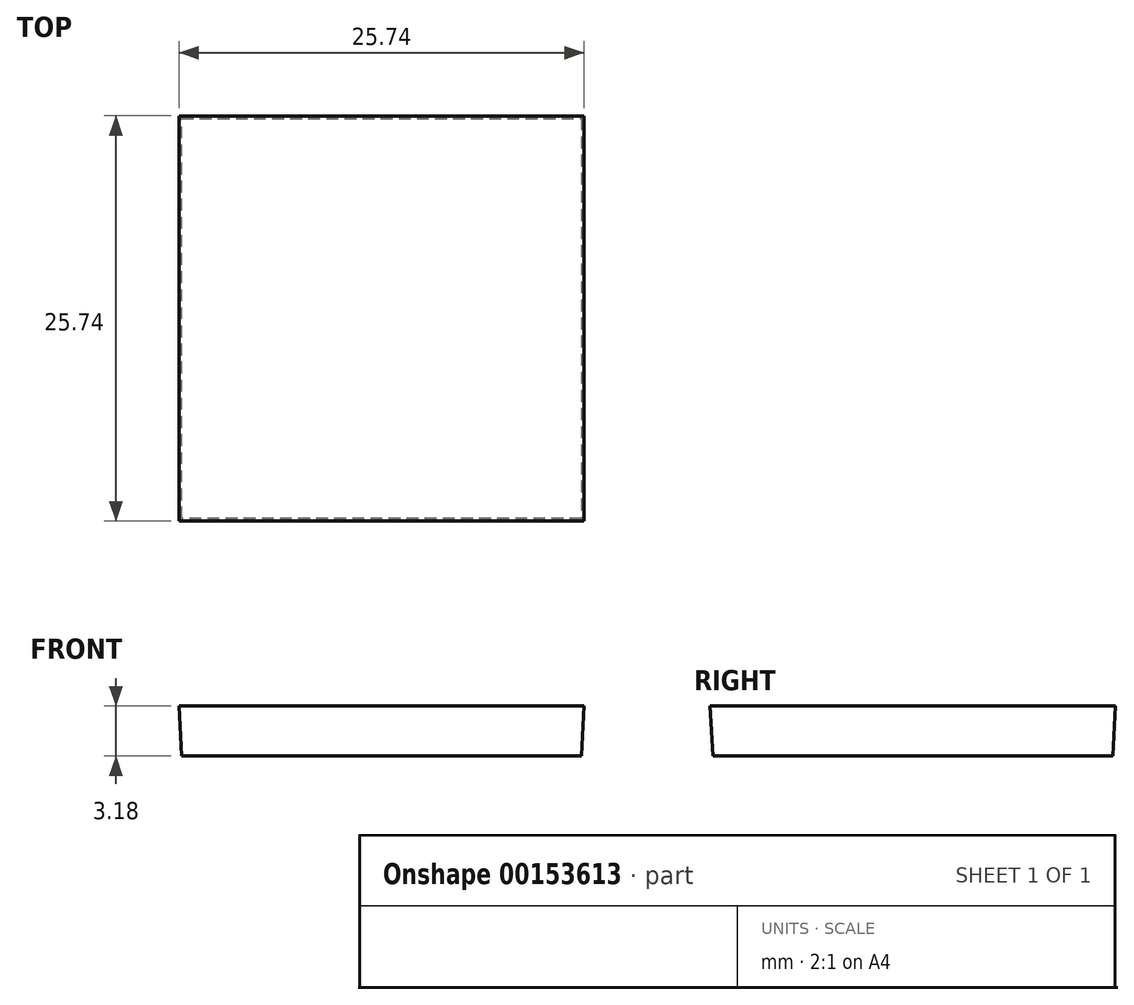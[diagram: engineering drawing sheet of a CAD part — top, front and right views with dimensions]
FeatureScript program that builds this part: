
annotation { "Feature Type Name" : "Feature", "Feature Type Description" : "" }
export const myFeature = defineFeature(function(context is Context, id is Id, definition is map)
    precondition{}
    {
        {
            var Q0;
            Q0=qCreatedBy(makeId("Top.planeOp"),FACE);
            var sketch = newSketch(context, id + "F0", { "sketchPlane" : qUnion([Q0])});
            skLineSegment(sketch, "E0.bottom", {"start": v(-12.7, 12.7) * mm, "end": v(12.7, 12.7) * mm});
            skLineSegment(sketch, "E0.top", {"start": v(-12.7, -12.7) * mm, "end": v(12.7, -12.7) * mm});
            skLineSegment(sketch, "E0.left", {"start": v(-12.7, 12.7) * mm, "end": v(-12.7, -12.7) * mm});
            skLineSegment(sketch, "E0.right", {"start": v(12.7, 12.7) * mm, "end": v(12.7, -12.7) * mm});
            skPoint(sketch, "E0.middle", {"position": v(0, 0) * mm});
            skSolve(sketch);
        }
        {
            var Q0;
            Q0 = qSketchRegion(id + "F0", true);
            extrude(context, id + "F1", {"entities" : qUnion([Q0]), "depth" : 3.17 * mm, "hasDraft" : true, "draftAngle" : 3 * degree});
        }
    });
